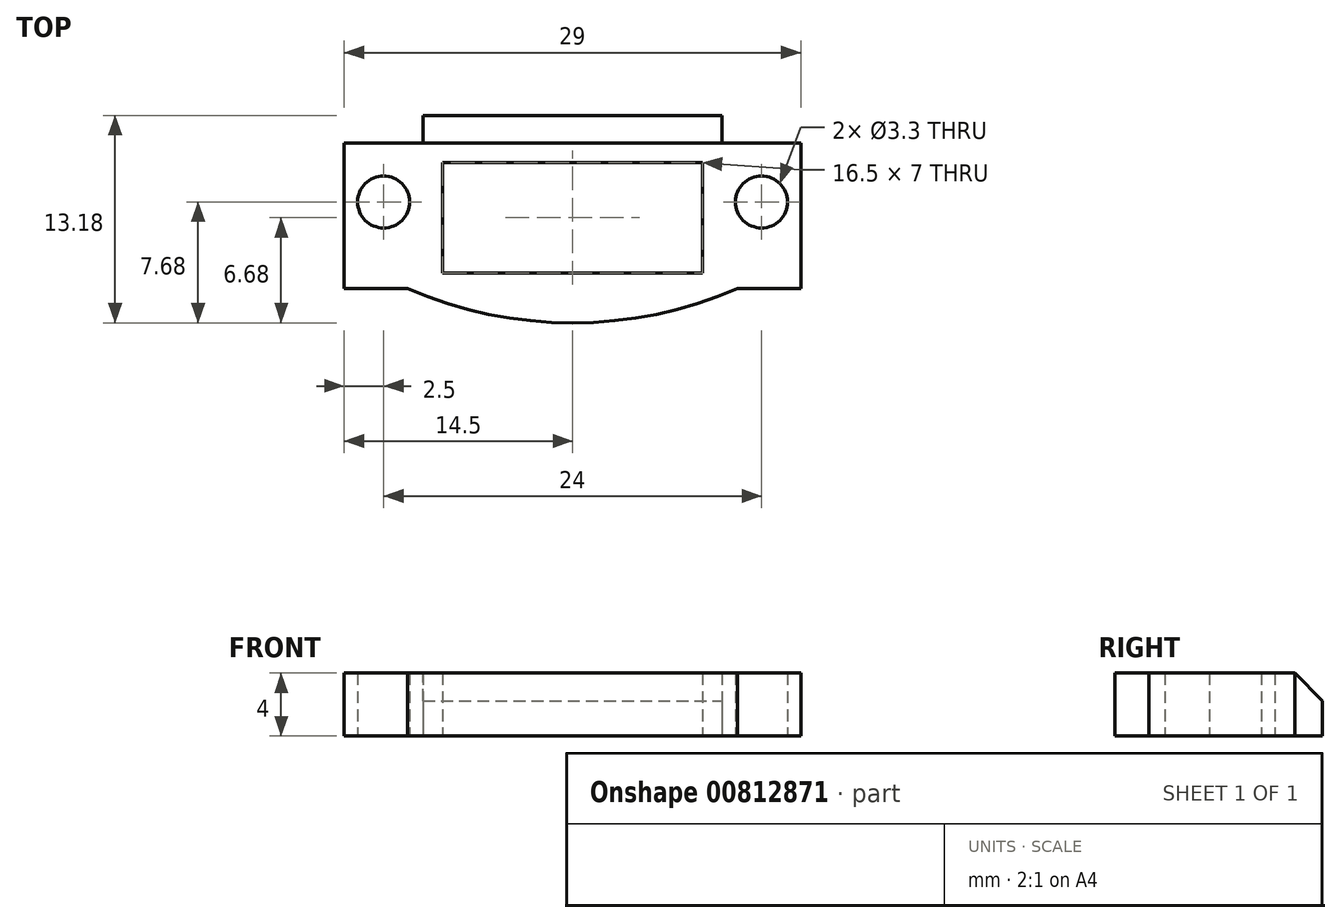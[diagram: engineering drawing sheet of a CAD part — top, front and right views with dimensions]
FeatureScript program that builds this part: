
annotation { "Feature Type Name" : "Feature", "Feature Type Description" : "" }
export const myFeature = defineFeature(function(context is Context, id is Id, definition is map)
    precondition{}
    {
        {
            var Q0;
            Q0=qCreatedBy(makeId("Top.planeOp"),FACE);
            var sketch = newSketch(context, id + "F0", { "sketchPlane" : qUnion([Q0])});
            skLineSegment(sketch, "E0.top", {"start": v(14.5, -5.5) * mm, "end": v(10.48, -5.5) * mm});
            skLineSegment(sketch, "E0.right", {"start": v(-14.5, 3.75) * mm, "end": v(-14.5, -5.5) * mm});
            skPoint(sketch, "E0.middle", {"position": v(0, 0) * mm});
            skCircle(sketch, "E1", {"center": v(-12, 0) * mm, "radius": 1.65 * mm});
            skLineSegment(sketch, "E2", {"start": v(-14.5, 3.75) * mm, "end": v(-9.5, 3.75) * mm});
            skLineSegment(sketch, "E3", {"start": v(-9.5, 3.75) * mm, "end": v(-9.5, 5.5) * mm});
            skLineSegment(sketch, "E4.MirrorCS", {"start": v(9.5, 3.75) * mm, "end": v(9.5, 5.5) * mm});
            skLineSegment(sketch, "E5.MirrorCS", {"start": v(14.5, 3.75) * mm, "end": v(9.5, 3.75) * mm});
            skLineSegment(sketch, "E6.MirrorCS", {"start": v(14.5, 3.75) * mm, "end": v(14.5, -5.5) * mm});
            skCircle(sketch, "E7.MirrorC", {"center": v(12, 0) * mm, "radius": 1.65 * mm});
            skLineSegment(sketch, "E8", {"start": v(-9.5, 5.5) * mm, "end": v(9.5, 5.5) * mm});
            skLineSegment(sketch, "E9", {"start": v(-8.25, -4.5) * mm, "end": v(8.25, -4.5) * mm});
            skLineSegment(sketch, "E10", {"start": v(-8.25, 2.5) * mm, "end": v(8.25, 2.5) * mm});
            skLineSegment(sketch, "E11", {"start": v(-8.25, 2.5) * mm, "end": v(-8.25, -4.5) * mm});
            skLineSegment(sketch, "E12", {"start": v(8.25, 2.5) * mm, "end": v(8.25, -4.5) * mm});
            skPoint(sketch, "E13", {"position": v(-10.48, -5.5) * mm});
            skPoint(sketch, "E14.MirrorP", {"position": v(10.48, -5.5) * mm});
            skArc(sketch, "E15", {"start": v(-10.48, -5.5) * mm, "mid": v(0, -7.68) * mm, "end": v(10.48, -5.5) * mm});
            skLineSegment(sketch, "E16.trimOffspring", {"start": v(-10.48, -5.5) * mm, "end": v(-14.5, -5.5) * mm});
            skSolve(sketch);
        }
        {
            var Q0;
            Q0=makeQuery(id+"F0.imprint","IMPRINT",FACE,{"disambiguationData":[TD([[makeQuery(id+"F0.imprint","IMPRINT",EDGE,{"derivedFrom":sQuery(id+"F0.wireOp",EDGE,"E0.top")}),-1.0]])]});
            extrude(context, id + "F1", {"entities" : qUnion([Q0]), "depth" : 4 * mm, "offsetDistance" : 25 * mm});
        }
        {
            var Q0;
            Q0=makeQuery(id+"F1.opExtrude","CAP_EDGE",EDGE,{"disambiguationData":[OSD([sQuery(id+"F0.wireOp",EDGE,"E8")])],"isStart":false});
            chamfer(context, id + "F2", {"entities" : qUnion([Q0]), "width" : 1.75 * mm, "tangentPropagation" : true});
        }
    });
